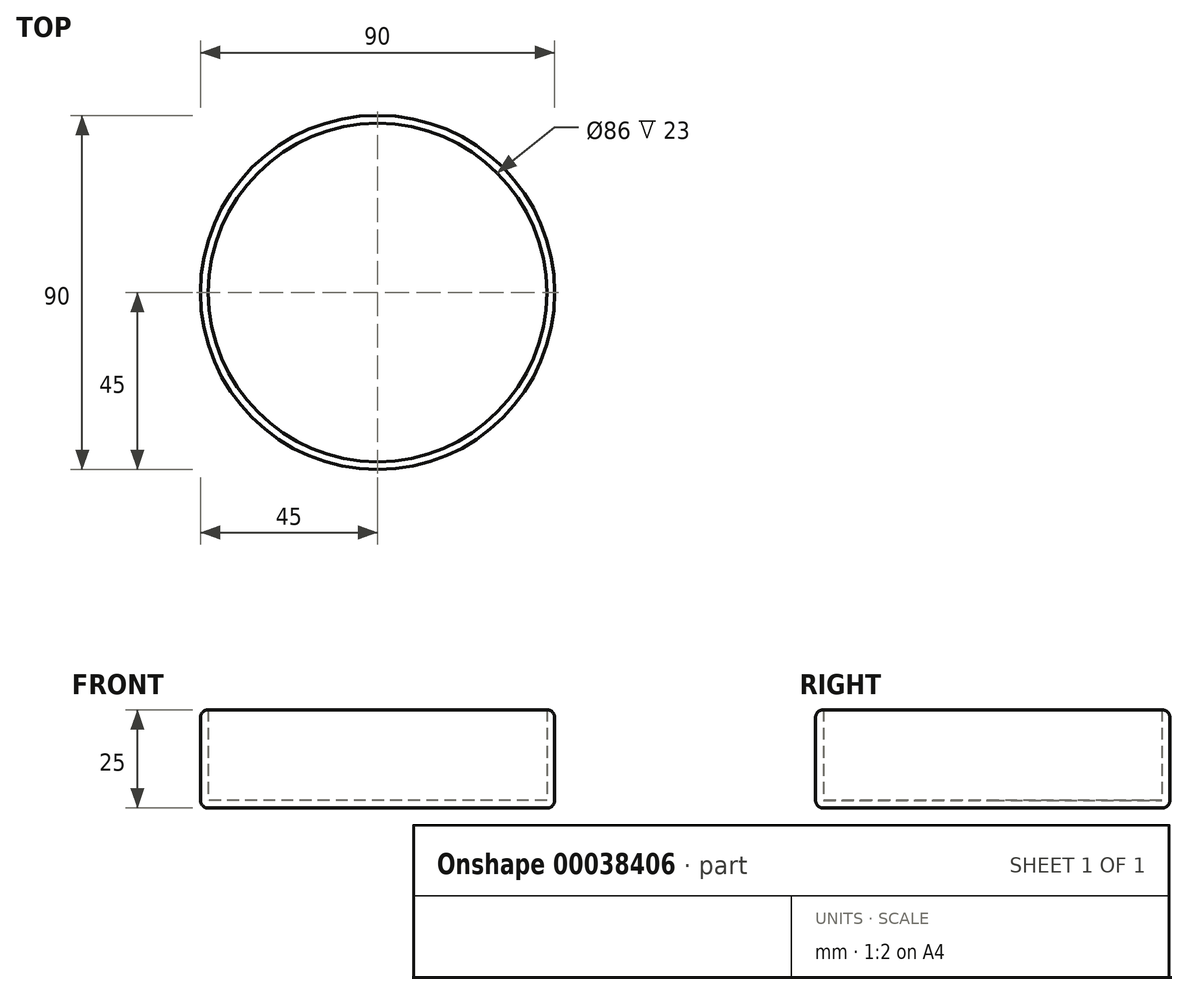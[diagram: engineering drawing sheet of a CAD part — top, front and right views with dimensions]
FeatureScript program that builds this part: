
annotation { "Feature Type Name" : "Feature", "Feature Type Description" : "" }
export const myFeature = defineFeature(function(context is Context, id is Id, definition is map)
    precondition{}
    {
        {
            var Q0;
            Q0=qCreatedBy(makeId("Top.planeOp"),FACE);
            var sketch = newSketch(context, id + "F0", { "sketchPlane" : qUnion([Q0])});
            skCircle(sketch, "E0", {"center": v(0, 0) * mm, "radius": 45 * mm});
            skCircle(sketch, "E1", {"center": v(0, 0) * mm, "radius": 43 * mm});
            skSolve(sketch);
        }
        {
            var Q0;
            Q0=makeQuery(id+"F0.imprint","IMPRINT",FACE,{"disambiguationData":[TD([[makeQuery(id+"F0.imprint","IMPRINT",EDGE,{"derivedFrom":sQuery(id+"F0.wireOp",EDGE,"E1")}),1.0]])]});
            extrude(context, id + "F1", {"entities" : qUnion([Q0]), "depth" : 2 * mm});
        }
        {
            var Q0;
            Q0=makeQuery(id+"F0.imprint","IMPRINT",FACE,{"disambiguationData":[TD([[makeQuery(id+"F0.imprint","IMPRINT",EDGE,{"derivedFrom":sQuery(id+"F0.wireOp",EDGE,"E0")}),1.0]])]});
            extrude(context, id + "F2", {"entities" : qUnion([Q0]), "operationType" : NewBodyOperationType.ADD, "depth" : 25 * mm});
        }
        {
            var Q0;
            Q0=makeQuery(id+"F2.opExtrude","CAP_EDGE",EDGE,{"disambiguationData":[OSD([sQuery(id+"F0.wireOp",EDGE,"E0")])],"isStart":true});
            var Q1;
            Q1=makeQuery(id+"F2.opExtrude","CAP_EDGE",EDGE,{"disambiguationData":[OSD([sQuery(id+"F0.wireOp",EDGE,"E0")])],"isStart":false});
            fillet(context, id + "F3", {"entities" : qUnion([Q0, Q1]), "radius" : 2 * mm, "tangentPropagation" : true, "allowEdgeOverflow" : false});
        }
    });
